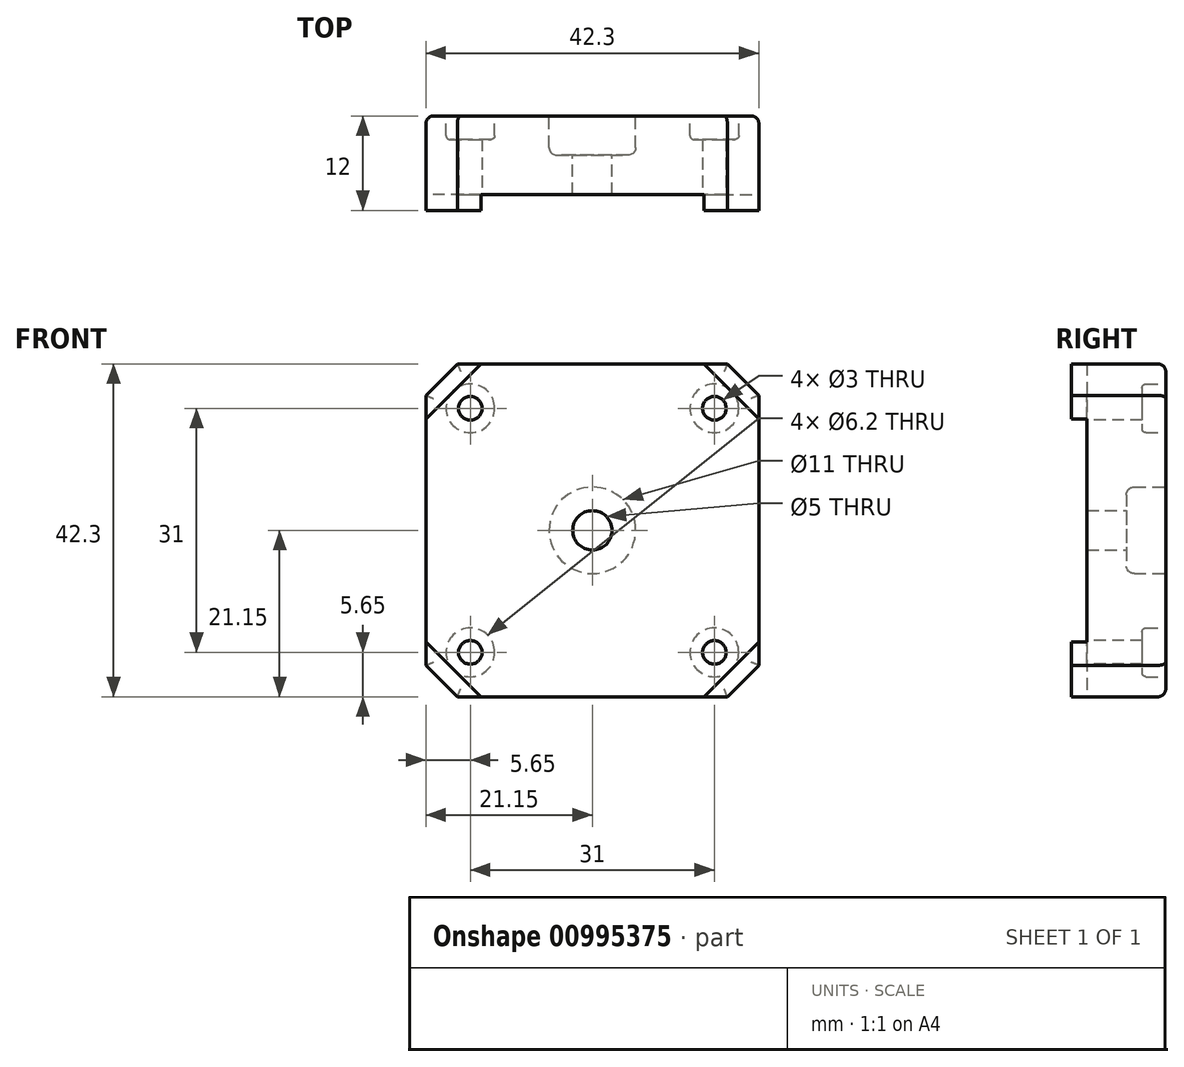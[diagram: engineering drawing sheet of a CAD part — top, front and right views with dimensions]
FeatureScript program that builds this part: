
annotation { "Feature Type Name" : "Feature", "Feature Type Description" : "" }
export const myFeature = defineFeature(function(context is Context, id is Id, definition is map)
    precondition{}
    {
        {
            var Q0;
            Q0=qCreatedBy(makeId("Front.planeOp"),FACE);
            var sketch = newSketch(context, id + "F0", { "sketchPlane" : qUnion([Q0])});
            skLineSegment(sketch, "E0.bottom", {"start": v(17.15, 21.15) * mm, "end": v(-17.15, 21.15) * mm});
            skLineSegment(sketch, "E0.top", {"start": v(17.15, -21.15) * mm, "end": v(-17.15, -21.15) * mm});
            skLineSegment(sketch, "E0.left", {"start": v(21.15, 17.15) * mm, "end": v(21.15, -17.15) * mm});
            skLineSegment(sketch, "E0.right", {"start": v(-21.15, 17.15) * mm, "end": v(-21.15, -17.15) * mm});
            skPoint(sketch, "E0.middle", {"position": v(0, 0) * mm});
            skLineSegment(sketch, "E1", {"start": v(-17.15, 21.15) * mm, "end": v(-21.15, 17.15) * mm});
            skPoint(sketch, "E2.orphan", {"position": v(-21.15, 21.15) * mm});
            skLineSegment(sketch, "E3.1.0", {"start": v(-21.15, -17.15) * mm, "end": v(-17.15, -21.15) * mm});
            skLineSegment(sketch, "E3.2.0", {"start": v(17.15, -21.15) * mm, "end": v(21.15, -17.15) * mm});
            skLineSegment(sketch, "E3.3.0", {"start": v(21.15, 17.15) * mm, "end": v(17.15, 21.15) * mm});
            skPoint(sketch, "E4.orphan", {"position": v(21.15, 21.15) * mm});
            skPoint(sketch, "E5.orphan", {"position": v(21.15, -21.15) * mm});
            skPoint(sketch, "E6.orphan", {"position": v(-21.15, -21.15) * mm});
            skSolve(sketch);
        }
        {
            var Q0;
            Q0=makeQuery(id+"F0.imprint","IMPRINT",FACE,{"disambiguationData":[TD([[makeQuery(id+"F0.imprint","IMPRINT",EDGE,{"derivedFrom":sQuery(id+"F0.wireOp",EDGE,"E0.bottom")}),1.0]])]});
            extrude(context, id + "F1", {"entities" : qUnion([Q0]), "depth" : 12 * mm, "offsetDistance" : 25 * mm});
        }
        {
            var Q0;
            Q0=makeQuery(id+"F1.opExtrude","CAP_FACE",FACE,{"disambiguationData":[OSD([sQuery(id+"F0.wireOp",EDGE,"E0.bottom"),sQuery(id+"F0.wireOp",EDGE,"E0.top"),sQuery(id+"F0.wireOp",EDGE,"E0.left"),sQuery(id+"F0.wireOp",EDGE,"E0.right"),sQuery(id+"F0.wireOp",EDGE,"E1"),sQuery(id+"F0.wireOp",EDGE,"E3.1.0"),sQuery(id+"F0.wireOp",EDGE,"E3.2.0"),sQuery(id+"F0.wireOp",EDGE,"E3.3.0")])],"isStart":false});
            var sketch = newSketch(context, id + "F2", { "sketchPlane" : qUnion([Q0])});
            skLineSegment(sketch, "E7.bottom", {"start": v(14.15, 21.15) * mm, "end": v(-14.15, 21.15) * mm});
            skLineSegment(sketch, "E7.top", {"start": v(14.15, -21.15) * mm, "end": v(-14.15, -21.15) * mm});
            skLineSegment(sketch, "E7.left", {"start": v(21.15, 14.15) * mm, "end": v(21.15, -14.15) * mm});
            skLineSegment(sketch, "E7.right", {"start": v(-21.15, 14.15) * mm, "end": v(-21.15, -14.15) * mm});
            skPoint(sketch, "E7.middle", {"position": v(0, 0) * mm});
            skLineSegment(sketch, "E8", {"start": v(-14.15, 21.15) * mm, "end": v(-21.15, 14.15) * mm});
            skLineSegment(sketch, "E9.1.0", {"start": v(-21.15, -14.15) * mm, "end": v(-14.15, -21.15) * mm});
            skLineSegment(sketch, "E9.2.0", {"start": v(14.15, -21.15) * mm, "end": v(21.15, -14.15) * mm});
            skLineSegment(sketch, "E9.3.0", {"start": v(21.15, 14.15) * mm, "end": v(14.15, 21.15) * mm});
            skPoint(sketch, "E10.orphan", {"position": v(-21.15, 21.15) * mm});
            skPoint(sketch, "E11.orphan", {"position": v(21.15, 21.15) * mm});
            skPoint(sketch, "E12.orphan", {"position": v(21.15, -21.15) * mm});
            skPoint(sketch, "E13.orphan", {"position": v(-21.15, -21.15) * mm});
            skSolve(sketch);
        }
        {
            var Q0;
            Q0 = qSketchRegion(id + "F2", true);
            extrude(context, id + "F3", {"entities" : qUnion([Q0]), "operationType" : NewBodyOperationType.REMOVE, "oppositeDirection" : true, "depth" : 2 * mm, "offsetDistance" : 25 * mm});
        }
        {
            var Q0;
            Q0=makeQuery(id+"F3.boolean.opBoolean","COPY",FACE,{"derivedFrom":makeQuery(id+"F3.opExtrude","CAP_FACE",FACE,{"disambiguationData":[OSD([sQuery(id+"F2.wireOp",EDGE,"E7.bottom"),sQuery(id+"F2.wireOp",EDGE,"E7.top"),sQuery(id+"F2.wireOp",EDGE,"E7.left"),sQuery(id+"F2.wireOp",EDGE,"E7.right"),sQuery(id+"F2.wireOp",EDGE,"E8"),sQuery(id+"F2.wireOp",EDGE,"E9.1.0"),sQuery(id+"F2.wireOp",EDGE,"E9.2.0"),sQuery(id+"F2.wireOp",EDGE,"E9.3.0")])],"isStart":false})});
            var sketch = newSketch(context, id + "F4", { "sketchPlane" : qUnion([Q0])});
            skLineSegment(sketch, "E14.bottom", {"start": v(15.5, 15.5) * mm, "end": v(-15.5, 15.5) * mm, "construction": true});
            skLineSegment(sketch, "E14.top", {"start": v(15.5, -15.5) * mm, "end": v(-15.5, -15.5) * mm, "construction": true});
            skLineSegment(sketch, "E14.left", {"start": v(15.5, 15.5) * mm, "end": v(15.5, -15.5) * mm, "construction": true});
            skLineSegment(sketch, "E14.right", {"start": v(-15.5, 15.5) * mm, "end": v(-15.5, -15.5) * mm, "construction": true});
            skPoint(sketch, "E14.middle", {"position": v(0, 0) * mm});
            skCircle(sketch, "E15", {"center": v(-15.5, 15.5) * mm, "radius": 1.5 * mm});
            skCircle(sketch, "E16.1.0", {"center": v(-15.5, -15.5) * mm, "radius": 1.5 * mm});
            skCircle(sketch, "E16.2.0", {"center": v(15.5, -15.5) * mm, "radius": 1.5 * mm});
            skCircle(sketch, "E16.3.0", {"center": v(15.5, 15.5) * mm, "radius": 1.5 * mm});
            skSolve(sketch);
        }
        {
            var Q0;
            Q0 = qSketchRegion(id + "F4", true);
            extrude(context, id + "F5", {"entities" : qUnion([Q0]), "operationType" : NewBodyOperationType.REMOVE, "endBound" : BoundingType.THROUGH_ALL, "oppositeDirection" : true, "depth" : 25 * mm, "offsetDistance" : 25 * mm});
        }
        {
            var Q0;
            Q0=makeQuery(id+"F1.opExtrude","CAP_FACE",FACE,{"disambiguationData":[OSD([sQuery(id+"F0.wireOp",EDGE,"E0.bottom"),sQuery(id+"F0.wireOp",EDGE,"E0.top"),sQuery(id+"F0.wireOp",EDGE,"E0.left"),sQuery(id+"F0.wireOp",EDGE,"E0.right"),sQuery(id+"F0.wireOp",EDGE,"E1"),sQuery(id+"F0.wireOp",EDGE,"E3.1.0"),sQuery(id+"F0.wireOp",EDGE,"E3.2.0"),sQuery(id+"F0.wireOp",EDGE,"E3.3.0")])],"isStart":true});
            var sketch = newSketch(context, id + "F6", { "sketchPlane" : qUnion([Q0])});
            skLineSegment(sketch, "E17.bottom", {"start": v(15.5, 15.5) * mm, "end": v(-15.5, 15.5) * mm, "construction": true});
            skLineSegment(sketch, "E17.top", {"start": v(15.5, -15.5) * mm, "end": v(-15.5, -15.5) * mm, "construction": true});
            skLineSegment(sketch, "E17.left", {"start": v(15.5, 15.5) * mm, "end": v(15.5, -15.5) * mm, "construction": true});
            skLineSegment(sketch, "E17.right", {"start": v(-15.5, 15.5) * mm, "end": v(-15.5, -15.5) * mm, "construction": true});
            skPoint(sketch, "E17.middle", {"position": v(0, 0) * mm});
            skCircle(sketch, "E18", {"center": v(-15.5, 15.5) * mm, "radius": 3.1 * mm});
            skCircle(sketch, "E19.1.0", {"center": v(-15.5, -15.5) * mm, "radius": 3.1 * mm});
            skCircle(sketch, "E19.2.0", {"center": v(15.5, -15.5) * mm, "radius": 3.1 * mm});
            skCircle(sketch, "E19.3.0", {"center": v(15.5, 15.5) * mm, "radius": 3.1 * mm});
            skSolve(sketch);
        }
        {
            var Q0;
            Q0 = qSketchRegion(id + "F6", true);
            extrude(context, id + "F7", {"entities" : qUnion([Q0]), "operationType" : NewBodyOperationType.REMOVE, "oppositeDirection" : true, "depth" : 3 * mm, "offsetDistance" : 25 * mm});
        }
        {
            var Q0;
            Q0=makeQuery(id+"F1.opExtrude","CAP_EDGE",EDGE,{"disambiguationData":[OSD([sQuery(id+"F0.wireOp",EDGE,"E0.bottom")])],"isStart":true});
            var Q1;
            Q1=makeQuery(id+"F1.opExtrude","CAP_EDGE",EDGE,{"disambiguationData":[OSD([sQuery(id+"F0.wireOp",EDGE,"E1")])],"isStart":true});
            var Q2;
            Q2=makeQuery(id+"F1.opExtrude","CAP_EDGE",EDGE,{"disambiguationData":[OSD([sQuery(id+"F0.wireOp",EDGE,"E0.right")])],"isStart":true});
            var Q3;
            Q3=makeQuery(id+"F1.opExtrude","CAP_EDGE",EDGE,{"disambiguationData":[OSD([sQuery(id+"F0.wireOp",EDGE,"E3.1.0")])],"isStart":true});
            var Q4;
            Q4=makeQuery(id+"F1.opExtrude","CAP_EDGE",EDGE,{"disambiguationData":[OSD([sQuery(id+"F0.wireOp",EDGE,"E0.top")])],"isStart":true});
            var Q5;
            Q5=makeQuery(id+"F1.opExtrude","CAP_EDGE",EDGE,{"disambiguationData":[OSD([sQuery(id+"F0.wireOp",EDGE,"E3.2.0")])],"isStart":true});
            var Q6;
            Q6=makeQuery(id+"F1.opExtrude","CAP_EDGE",EDGE,{"disambiguationData":[OSD([sQuery(id+"F0.wireOp",EDGE,"E0.left")])],"isStart":true});
            var Q7;
            Q7=makeQuery(id+"F1.opExtrude","CAP_EDGE",EDGE,{"disambiguationData":[OSD([sQuery(id+"F0.wireOp",EDGE,"E3.3.0")])],"isStart":true});
            fillet(context, id + "F8", {"entities" : qUnion([Q0, Q1, Q2, Q3, Q4, Q5, Q6, Q7]), "radius" : 1 * mm, "tangentPropagation" : true, "allowEdgeOverflow" : false});
        }
        {
            var Q0;
            Q0=makeQuery(id+"F7.boolean.opBoolean","COPY",EDGE,{"derivedFrom":makeQuery(id+"F7.opExtrude","CAP_EDGE",EDGE,{"disambiguationData":[OSD([sQuery(id+"F6.wireOp",EDGE,"E19.3.0")])],"isStart":true})});
            var Q1;
            Q1=makeQuery(id+"F7.boolean.opBoolean","COPY",EDGE,{"derivedFrom":makeQuery(id+"F7.opExtrude","CAP_EDGE",EDGE,{"disambiguationData":[OSD([sQuery(id+"F6.wireOp",EDGE,"E19.3.0")])],"isStart":false})});
            var Q2;
            Q2=makeQuery(id+"F7.boolean.opBoolean","COPY",EDGE,{"derivedFrom":makeQuery(id+"F7.opExtrude","CAP_EDGE",EDGE,{"disambiguationData":[OSD([sQuery(id+"F6.wireOp",EDGE,"E18")])],"isStart":true})});
            var Q3;
            Q3=makeQuery(id+"F7.boolean.opBoolean","COPY",EDGE,{"derivedFrom":makeQuery(id+"F7.opExtrude","CAP_EDGE",EDGE,{"disambiguationData":[OSD([sQuery(id+"F6.wireOp",EDGE,"E18")])],"isStart":false})});
            var Q4;
            Q4=makeQuery(id+"F7.boolean.opBoolean","COPY",EDGE,{"derivedFrom":makeQuery(id+"F7.opExtrude","CAP_EDGE",EDGE,{"disambiguationData":[OSD([sQuery(id+"F6.wireOp",EDGE,"E19.2.0")])],"isStart":true})});
            var Q5;
            Q5=makeQuery(id+"F7.boolean.opBoolean","COPY",EDGE,{"derivedFrom":makeQuery(id+"F7.opExtrude","CAP_EDGE",EDGE,{"disambiguationData":[OSD([sQuery(id+"F6.wireOp",EDGE,"E19.2.0")])],"isStart":false})});
            var Q6;
            Q6=makeQuery(id+"F7.boolean.opBoolean","COPY",EDGE,{"derivedFrom":makeQuery(id+"F7.opExtrude","CAP_EDGE",EDGE,{"disambiguationData":[OSD([sQuery(id+"F6.wireOp",EDGE,"E19.1.0")])],"isStart":true})});
            var Q7;
            Q7=makeQuery(id+"F7.boolean.opBoolean","COPY",EDGE,{"derivedFrom":makeQuery(id+"F7.opExtrude","CAP_EDGE",EDGE,{"disambiguationData":[OSD([sQuery(id+"F6.wireOp",EDGE,"E19.1.0")])],"isStart":false})});
            fillet(context, id + "F9", {"entities" : qUnion([Q0, Q1, Q2, Q3, Q4, Q5, Q6, Q7]), "radius" : .5 * mm, "tangentPropagation" : true, "allowEdgeOverflow" : false});
        }
        {
            var Q0;
            Q0=makeQuery(id+"F1.opExtrude","CAP_FACE",FACE,{"disambiguationData":[OSD([sQuery(id+"F0.wireOp",EDGE,"E0.bottom"),sQuery(id+"F0.wireOp",EDGE,"E0.top"),sQuery(id+"F0.wireOp",EDGE,"E0.left"),sQuery(id+"F0.wireOp",EDGE,"E0.right"),sQuery(id+"F0.wireOp",EDGE,"E1"),sQuery(id+"F0.wireOp",EDGE,"E3.1.0"),sQuery(id+"F0.wireOp",EDGE,"E3.2.0"),sQuery(id+"F0.wireOp",EDGE,"E3.3.0")])],"isStart":true});
            var sketch = newSketch(context, id + "F10", { "sketchPlane" : qUnion([Q0])});
            skCircle(sketch, "E20", {"center": v(0, 0) * mm, "radius": 5.5 * mm});
            skSolve(sketch);
        }
        {
            var Q0;
            Q0 = qSketchRegion(id + "F10", true);
            extrude(context, id + "F11", {"entities" : qUnion([Q0]), "operationType" : NewBodyOperationType.REMOVE, "oppositeDirection" : true, "depth" : 5 * mm, "offsetDistance" : 25 * mm});
        }
        {
            var Q0;
            Q0=makeQuery(id+"F11.boolean.opBoolean","COPY",FACE,{"derivedFrom":makeQuery(id+"F11.opExtrude","CAP_FACE",FACE,{"disambiguationData":[OSD([sQuery(id+"F10.wireOp",EDGE,"E20")])],"isStart":false})});
            var sketch = newSketch(context, id + "F12", { "sketchPlane" : qUnion([Q0])});
            skCircle(sketch, "E21", {"center": v(0, 0) * mm, "radius": 2.5 * mm});
            skSolve(sketch);
        }
        {
            var Q0;
            Q0 = qSketchRegion(id + "F12", true);
            extrude(context, id + "F13", {"entities" : qUnion([Q0]), "operationType" : NewBodyOperationType.REMOVE, "endBound" : BoundingType.THROUGH_ALL, "oppositeDirection" : true, "depth" : 25 * mm, "offsetDistance" : 25 * mm});
        }
        {
            var Q0;
            Q0=makeQuery(id+"F11.boolean.opBoolean","COPY",EDGE,{"derivedFrom":makeQuery(id+"F11.opExtrude","CAP_EDGE",EDGE,{"disambiguationData":[OSD([sQuery(id+"F10.wireOp",EDGE,"E20")])],"isStart":true})});
            var Q1;
            Q1=makeQuery(id+"F11.boolean.opBoolean","COPY",EDGE,{"derivedFrom":makeQuery(id+"F11.opExtrude","CAP_EDGE",EDGE,{"disambiguationData":[OSD([sQuery(id+"F10.wireOp",EDGE,"E20")])],"isStart":false})});
            fillet(context, id + "F14", {"entities" : qUnion([Q0, Q1]), "radius" : 1 * mm, "tangentPropagation" : true, "allowEdgeOverflow" : false});
        }
    });
